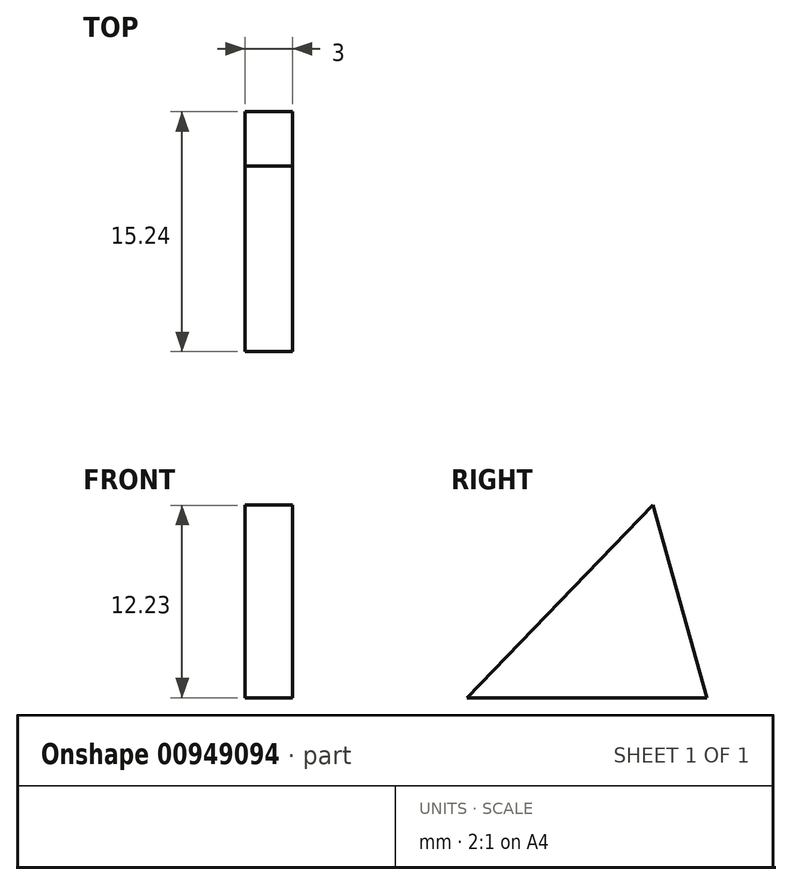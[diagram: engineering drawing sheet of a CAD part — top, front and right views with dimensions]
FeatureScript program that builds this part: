
annotation { "Feature Type Name" : "Feature", "Feature Type Description" : "" }
export const myFeature = defineFeature(function(context is Context, id is Id, definition is map)
    precondition{}
    {
        {
            var Q0;
            Q0=qCreatedBy(makeId("Right.planeOp"),FACE);
            var sketch = newSketch(context, id + "F0", { "sketchPlane" : qUnion([Q0])});
            skLineSegment(sketch, "E0", {"start": v(-28.58, 18.96) * mm, "end": v(-40.4, 6.73) * mm});
            skLineSegment(sketch, "E1", {"start": v(-40.4, 6.73) * mm, "end": v(-25.15, 6.73) * mm});
            skLineSegment(sketch, "E2", {"start": v(-25.15, 6.73) * mm, "end": v(-28.58, 18.96) * mm});
            skSolve(sketch);
        }
        {
            var Q0;
            Q0 = qSketchRegion(id + "F0", true);
            extrude(context, id + "F1", {"entities" : qUnion([Q0]), "depth" : 3 * mm, "offsetDistance" : 25.4 * mm});
        }
    });
